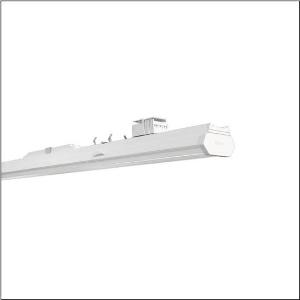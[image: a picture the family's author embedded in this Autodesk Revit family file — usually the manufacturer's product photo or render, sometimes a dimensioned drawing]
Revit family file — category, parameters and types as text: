
# Revit family: licross_r__21_protected_mo_52tp11mn4a5g_f46f
name_source: partatom
category: Lighting Fixtures
units: mm (PartAtom-declared; Revit-internal decimal feet)

## family parameters
Cut with Voids When Loaded = No
Host = Face
Light Source = No
Part Type = Normal
Room Calculation Point = No
Round Connector Dimension = Use Diameter
Shared = No

## types (1)
- --- (1 x LED, 10700 lm, 60.5 W, 4000K)
    Apparent Load = 61 VA
    CIE Flux Codes = 83 94 98 100 100
    Color Rendering = 80
    Color Temperature = 4000K
    Default Elevation = 1800 mm
    Description = Licross® 21 Protected MO, luminaire insert, of sheet steel, galvanised, coil coated, white, length: 1.500mm, width: 66mm, height: 67mm, LED rated luminous flux: 10.700lm, light colour: 840, SDCM (Standard Deviation of Colour Matching)MacAdam ≤ 3 SDCM (initial), control gear: ON/OFF Multilumen, with plug, 3-pole, with phase selection, mains connection: 220..240V, AC, 50/60Hz, rated input power: 61W, internal wiring halogen-free, primary light control with lens, of plastic, primary optical cover: cover, of PMMA, light emission: direct distribution, primary light characteristic: symmetric, protection rating (complete): IP64, insulation class (complete): insulation class I (protective earthing), certification: CE, ENEC, VDE, UKCA, protection symbol: D if used in an environment with conductive dust loads with corresponding accessories, impact resistance: IK06, permissible ambient temperature for indoor applications: -35..+45°C, corresponds to IFS (International Featured Standards) requirements for safety and quality in the food industry, reducing of maximum allowable ambient temperature of 5°C with ceiling mounting, LABS conformity tested according to VDMA 24364:2018-05, packaging unit: 1 piece
    Height = 92 mm
    Lamp = 1 x LED
    Lamp Light Flux = 10700 lm
    Lamp Power = 60.5 W
    Lamp count = 1
    Length = 1500 mm
    Luminous efficacy = 177 lm/W
    Manufacturer = Siteco
    ModVariant = No
    Model = 52TP11MN4A5G
    Mounting Place = Ceiling
    Mounting Type = Pendant
    Number of Poles = 1
    OnlyDefault = Yes
    Power Factor = 1
    Product Name = Licross® 21 Protected MO
    Product group = luminaire insert | ceiling pendant
    ProductGroupID = 901
    Protection Class = Protection class I
    Protection Degree = IP 64
    RLX_Detail_Level = 1
    RLX_Emergency_Light_Flux = 0 lm
    RLX_Emergency_Type = 0
    RLX_Emergency_Type_DB = No
    RlxData = <blob elided: 21941 chars, md5=9c02f341>
    Socket = socket
    Standby Power = 0 W
    System Light Flux = 10700 lm
    System Power = 61 W
    Type Comments = factory setting: luminous flux: 100 % | (A | C | E) | 140 mA
    Type Image = l_1256148.jpg
    URL = http://relux.com
    VarID = @adj_112965
    Voltage = 0 V
    Weight = 0.00 kg
    Width = 88 mm

## geometry (parser evidence)
native form markers: Blend x4, Sweep x11
no freeform markers — native parametric forms only
